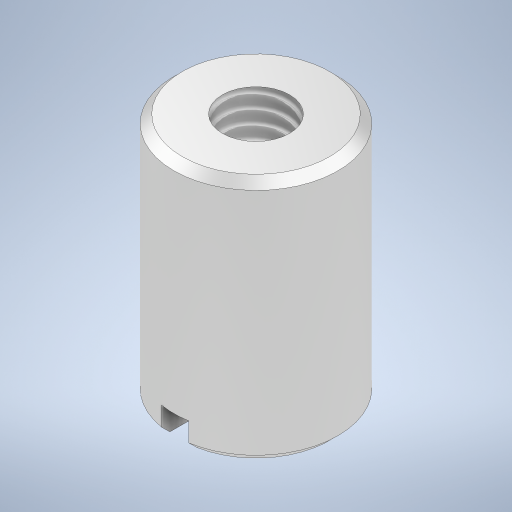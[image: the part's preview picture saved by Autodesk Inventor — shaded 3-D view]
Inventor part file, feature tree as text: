
AUTODESK INVENTOR PART (.ipt)
format: ipt  version: 2024.2 (Build 282272000, 272)  size: 305,664 bytes
history: native  units: mm
features: sketch x2, revolve x1, extrude x1, hole x1, chamfer x1
ambient origin geometry x8: Origin, YZ Plane, XZ Plane, XY Plane, X Axis, Y Axis, Z Axis, Center Point
bodies: Solid1 (feature_tree)
feature tree (6):
  revolve  "Revolution1"  [1 undecoded]
  sketch  "Sketch2"  dims[d5=90.0deg d6=1.0mm d7=1.0mm d8=0.0mm d9=2.459mm d10=6.0mm d11=4.0mm d12=2.0mm d13=90.0deg d14=6.0mm d15=0.0mm d18=0.3mm d19=2.0mm d20=45.0deg]
  extrude  "Extrusion1"  Depth=1.0mm
  hole  "Hole1"  [1 undecoded]
  chamfer  "Chamfer1"  Distance=0.3mm Angle=45.0deg
  sketch  "Sketch1"  dims[d2=9.0mm d4=6.0mm]
note: 2 required parameter values undecoded (feature->parameter linkage not recoverable at this tier; creation-order binding heuristic only, values carry confidence <= 0.55)